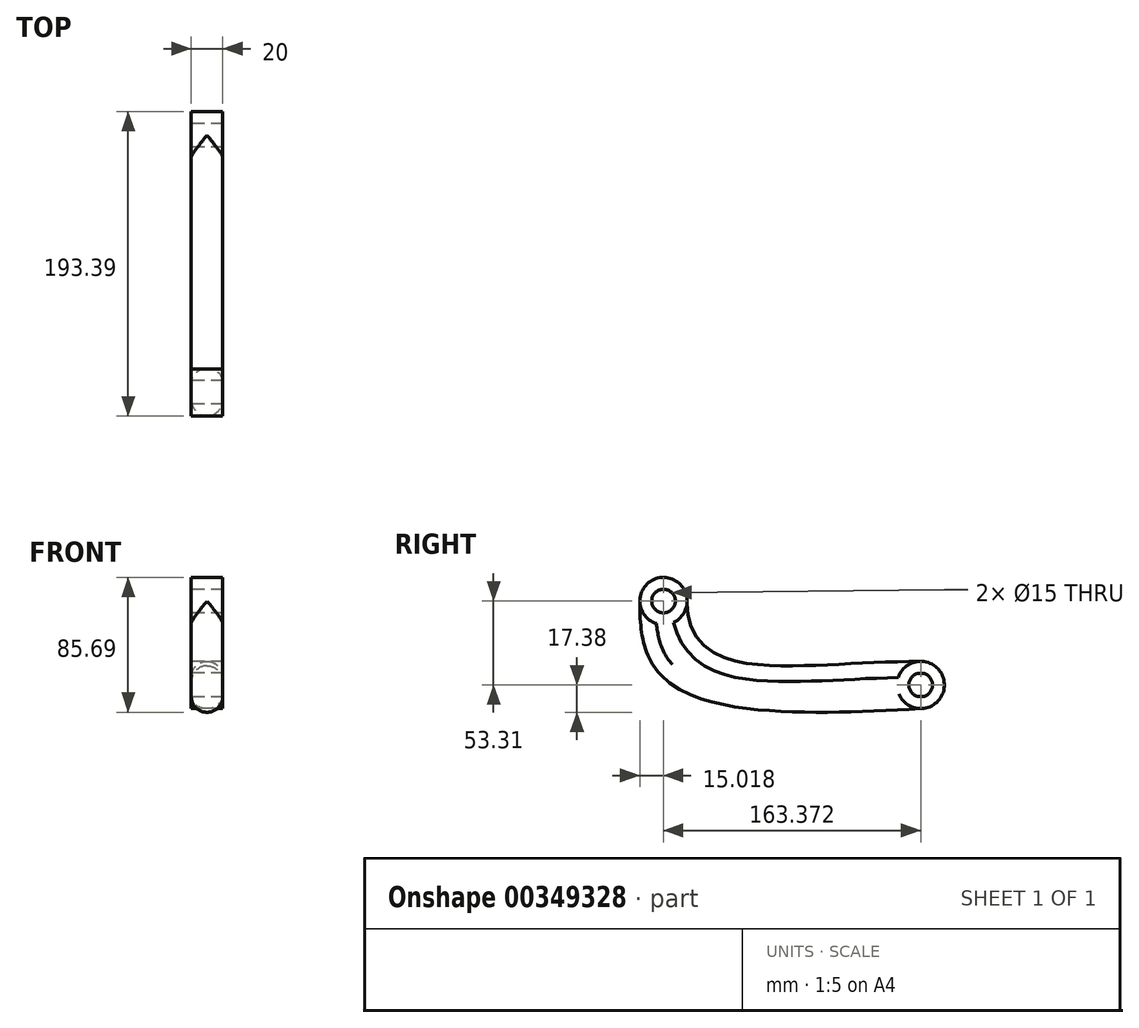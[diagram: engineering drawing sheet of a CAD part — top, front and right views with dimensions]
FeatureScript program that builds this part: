
annotation { "Feature Type Name" : "Feature", "Feature Type Description" : "" }
export const myFeature = defineFeature(function(context is Context, id is Id, definition is map)
    precondition{}
    {
        {
            var Q0;
            Q0=qCreatedBy(makeId("Right.planeOp"),FACE);
            var sketch = newSketch(context, id + "F0", { "sketchPlane" : qUnion([Q0])});
            skCircle(sketch, "E0", {"center": v(0, 0) * mm, "radius": 15 * mm});
            skCircle(sketch, "E1", {"center": v(0, 0) * mm, "radius": 7.5 * mm});
            skCircle(sketch, "E2", {"center": v(-163.37, 53.31) * mm, "radius": 15 * mm});
            skCircle(sketch, "E3", {"center": v(-163.37, 53.31) * mm, "radius": 7.5 * mm});
            skFitSpline(sketch, "E4", {"points": [v(-148.5, 55.23) * mm, v(0, 15) * mm], "startDerivative": vector(-1.3, -175.66) * mm, "endDerivative": vector(243.8, 1.03) * mm});
            skLineSegment(sketch, "E5", {"start": v(-165, 68.22) * mm, "end": v(-165, -15) * mm});
            skLineSegment(sketch, "E6", {"start": v(15, 0) * mm, "end": v(15, -15) * mm});
            skLineSegment(sketch, "E7", {"start": v(-149.95, 60) * mm, "end": v(0, 60) * mm});
            skFitSpline(sketch, "E8", {"points": [v(-178.35, 54.19) * mm, v(0, -15) * mm], "startDerivative": vector(-3.82, -172.37) * mm, "endDerivative": vector(462.82, 30.24) * mm});
            skSolve(sketch);
        }
        {
            var Q0;
            Q0 = qSketchRegion(id + "F0", true);
            extrude(context, id + "F1", {"entities" : qUnion([Q0]), "endBound" : BoundingType.SYMMETRIC, "depth" : 20 * mm});
        }
        {
            var Q0;
            Q0=makeQuery(id+"F1.opExtrude","CAP_EDGE",EDGE,{"disambiguationData":[OSD([sQuery(id+"F0.wireOp",EDGE,"e5852107-563b-4547-9463-1571bc91e50c")])],"isStart":true});
            var Q1;
            Q1=makeQuery(id+"F1.opExtrude","CAP_EDGE",EDGE,{"disambiguationData":[OSD([sQuery(id+"F0.wireOp",EDGE,"e5852107-563b-4547-9463-1571bc91e50c")])],"isStart":false});
            var Q2;
            Q2=makeQuery(id+"F1.opExtrude","CAP_EDGE",EDGE,{"disambiguationData":[OSD([sQuery(id+"F0.wireOp",EDGE,"E4")])],"isStart":false});
            var Q3;
            Q3=makeQuery(id+"F1.opExtrude","CAP_EDGE",EDGE,{"disambiguationData":[OSD([sQuery(id+"F0.wireOp",EDGE,"E4")])],"isStart":true});
            var Q4;
            Q4=makeQuery(id+"F1.opExtrude","CAP_EDGE",EDGE,{"disambiguationData":[OSD([sQuery(id+"F0.wireOp",EDGE,"E8")])],"isStart":false});
            var Q5;
            Q5=makeQuery(id+"F1.opExtrude","CAP_EDGE",EDGE,{"disambiguationData":[OSD([sQuery(id+"F0.wireOp",EDGE,"E8")])],"isStart":true});
            fillet(context, id + "F2", {"entities" : qUnion([Q0, Q1, Q2, Q3, Q4, Q5]), "radius" : 10 * mm, "tangentPropagation" : true, "allowEdgeOverflow" : false});
        }
    });
